# Revit family: NBS_BetafenceLimited_MtlMeshPnlFncngSym_ZenturoGabionWallBasePlated
name_source: partatom
category: Generic Models
revit_build: Autodesk Revit 2016 (Build: 20151007_0715(x64)
units: mm (PartAtom-declared; Revit-internal decimal feet)

## family parameters
Can host rebar = No
Cut with Voids When Loaded = No
OmniClass Number = 23.11.25.19.21
OmniClass Title = Panel Fences
Part Type = Normal
Room Calculation Point = No
Round Connector Dimension = Use Diameter
Shared = No
Work Plane-Based = No

## types (1)
- Zenturo Gabion Wall Baseplated
    AssetType = Fixed
    BIMObjectName = NBS_BetafenceLimited_MetalMeshPanelFencingSystem_ZenturoGabionWallBasePlated
    Category = Ss_25_14_67_51: Metal mesh panel fencing systems
    Diameter = 0 mm  [stored 0 ft]
    DurationUnit = year
    FoundationMaterial = NBS_Concept
    Has3FoldPanel = No
    Has4FoldPanel = Yes
    Height = 2005 mm  [stored 6.57808 ft]
    IfcExportAs = IfcWallType
    IfcExportType = NOTDEFINED
    IsExternal = Yes
    ManufacturerName = Betafence Limited
    ManufacturerURL = www.betafence.co.uk
    ModelReference = Zenturo Gabion Wall Baseplated
    NBSCertification = www.nationalbimlibrary.com/cert/mbcdywid
    NBSDescription = Metal mesh panel fencing system
    NBSReference = 25-20-30/145
    Name = MetalMeshPanelFencingSystem_ZenturoGabionWallBaseplated_BetafenceLimited
    NominalHeight = 2005 mm  [stored 6.57808 ft]
    NominalLength = 0 mm  [stored 0 ft]
    NominalWidth = 2005 mm  [stored 6.57808 ft]
    PanelElevation = 20 mm  [stored 0.0656168 ft]
    PanelHeight = 2005 mm  [stored 6.57808 ft]
    PanelMaterial = NBS_BetafenceLimited_MtlMeshPnlFncngSym_ZenturoGabionWall_Panel
    PanelOffsetFromPostAxis = 20 mm  [stored 0.0656168 ft]
    PanelOffsetFromPostCL = 72 mm  [stored 0.23622 ft]
    PanelSizeOptions = 2005 x 655 mm, 2005 x 955 mm, 2005 x 1255 mm, 2005 x 1555 mm, 2005 x 1705 mm, 2005 x 2005 mm
    PanelThickness = 144 mm  [stored 0.472441 ft]
    PostFoundations = Installation guides available on request
    PostHeight = 2005 mm  [stored 6.57808 ft]
    PostMaterial = NBS_Concept
    PostMountDepth = 700 mm  [stored 2.29659 ft]
    PostThickness = 120 mm  [stored 0.393701 ft]
    PostWidth = 40 mm  [stored 0.131234 ft]
    ProductInformation = //www.betafence.co.uk/en/zenturo-super-gabion-wall
    StandardPostAxisOffset = 2005 mm  [stored 6.57808 ft]
    Uniclass2015Code = Ss_25_14_67_51
    Uniclass2015Title = Metal mesh panel fencing systems
    Uniclass2015Version = Systems v1.6
    Version = 1
    WarrantyDurationUnit = year

note: [stored X ft] marks values corroborated as IEEE doubles in the binary element streams (Revit-internal decimal feet)

## geometry (parser evidence)
native form markers: Sweep x7
no freeform markers — native parametric forms only
